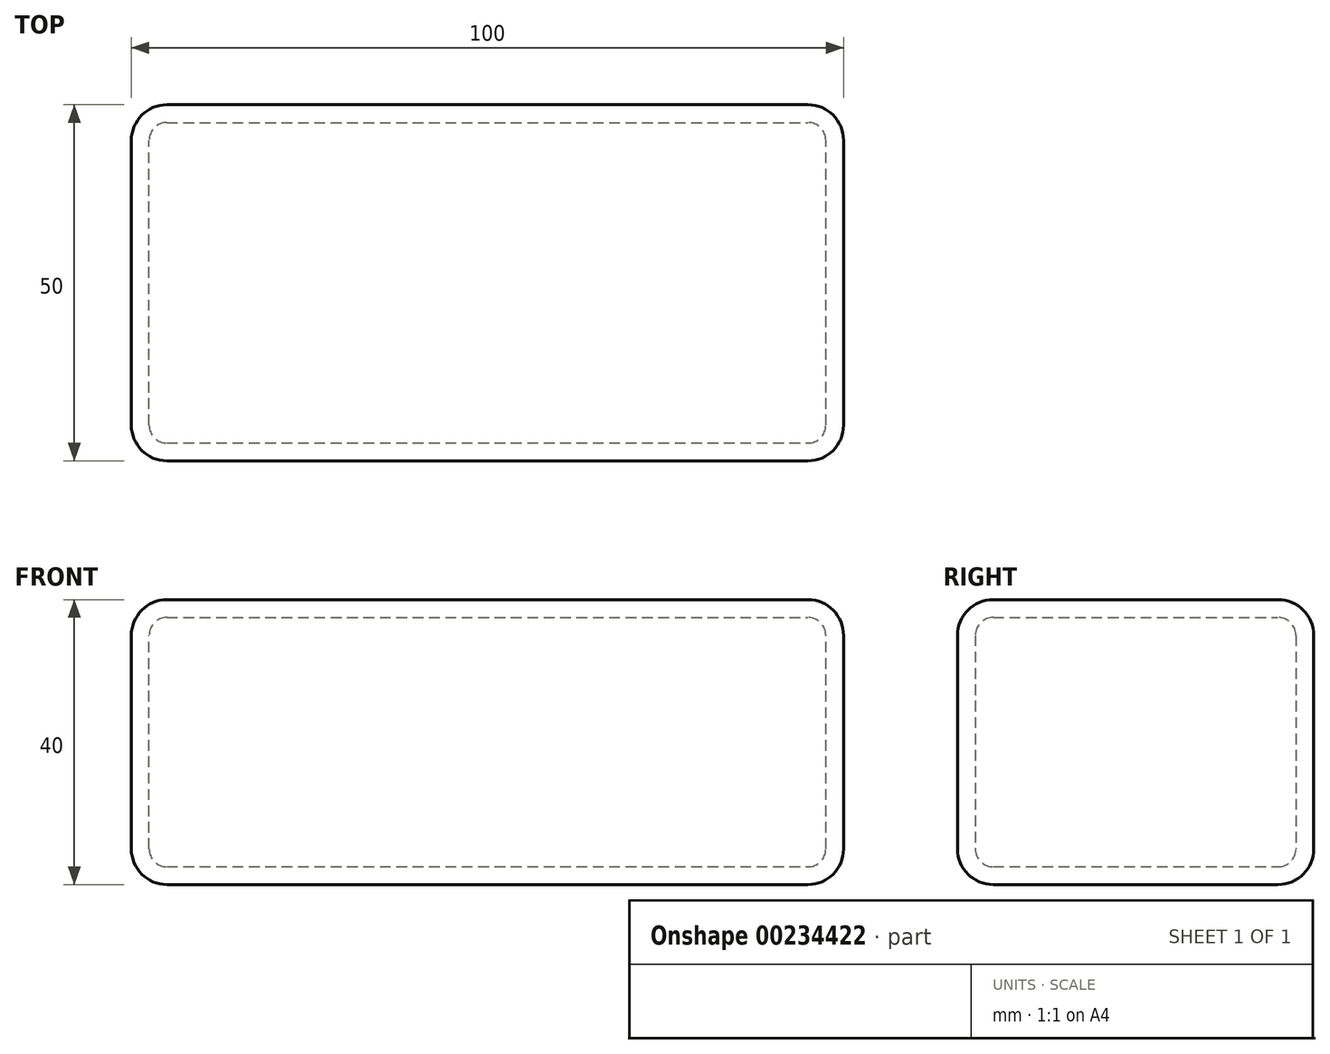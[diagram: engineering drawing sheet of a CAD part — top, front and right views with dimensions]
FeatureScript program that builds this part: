
annotation { "Feature Type Name" : "Feature", "Feature Type Description" : "" }
export const myFeature = defineFeature(function(context is Context, id is Id, definition is map)
    precondition{}
    {
        {
            var Q0;
            Q0=qCreatedBy(makeId("Top.planeOp"),FACE);
            var sketch = newSketch(context, id + "F0", { "sketchPlane" : qUnion([Q0])});
            skLineSegment(sketch, "E0.bottom", {"start": v(50, -25) * mm, "end": v(-50, -25) * mm});
            skLineSegment(sketch, "E0.top", {"start": v(50, 25) * mm, "end": v(-50, 25) * mm});
            skLineSegment(sketch, "E0.left", {"start": v(50, -25) * mm, "end": v(50, 25) * mm});
            skLineSegment(sketch, "E0.right", {"start": v(-50, -25) * mm, "end": v(-50, 25) * mm});
            skPoint(sketch, "E0.middle", {"position": v(0, 0) * mm});
            skSolve(sketch);
        }
        {
            var Q0;
            Q0=makeQuery(id+"F0.imprint","IMPRINT",FACE,{"disambiguationData":[TD([[makeQuery(id+"F0.imprint","IMPRINT",EDGE,{"derivedFrom":sQuery(id+"F0.wireOp",EDGE,"E0.bottom")}),-1.0]])]});
            extrude(context, id + "F1", {"entities" : qUnion([Q0]), "depth" : 20 * mm});
        }
        {
            var Q0;
            Q0=makeQuery(id+"F1.opExtrude","CAP_EDGE",EDGE,{"disambiguationData":[OSD([sQuery(id+"F0.wireOp",EDGE,"E0.right")])],"isStart":false});
            var Q1;
            Q1=makeQuery(id+"F1.opExtrude","CAP_EDGE",EDGE,{"disambiguationData":[OSD([sQuery(id+"F0.wireOp",EDGE,"E0.bottom")])],"isStart":false});
            var Q2;
            Q2=makeQuery(id+"F1.opExtrude","CAP_EDGE",EDGE,{"disambiguationData":[OSD([sQuery(id+"F0.wireOp",EDGE,"E0.left")])],"isStart":false});
            var Q3;
            Q3=makeQuery(id+"F1.opExtrude","CAP_EDGE",EDGE,{"disambiguationData":[OSD([sQuery(id+"F0.wireOp",EDGE,"E0.top")])],"isStart":false});
            var Q4;
            Q4=makeQuery(id+"F1.opExtrude","SWEPT_EDGE",EDGE,{"disambiguationData":[OSD([sQuery(id+"F0.wireOp",EDGE,"E0.top"),sQuery(id+"F0.wireOp",EDGE,"E0.left")])]});
            var Q5;
            Q5=makeQuery(id+"F1.opExtrude","SWEPT_EDGE",EDGE,{"disambiguationData":[OSD([sQuery(id+"F0.wireOp",EDGE,"E0.bottom"),sQuery(id+"F0.wireOp",EDGE,"E0.left")])]});
            var Q6;
            Q6=makeQuery(id+"F1.opExtrude","SWEPT_EDGE",EDGE,{"disambiguationData":[OSD([sQuery(id+"F0.wireOp",EDGE,"E0.bottom"),sQuery(id+"F0.wireOp",EDGE,"E0.right")])]});
            var Q7;
            Q7=makeQuery(id+"F1.opExtrude","SWEPT_EDGE",EDGE,{"disambiguationData":[OSD([sQuery(id+"F0.wireOp",EDGE,"E0.top"),sQuery(id+"F0.wireOp",EDGE,"E0.right")])]});
            fillet(context, id + "F2", {"entities" : qUnion([Q0, Q1, Q2, Q3, Q4, Q5, Q6, Q7]), "radius" : 5 * mm, "tangentPropagation" : true, "allowEdgeOverflow" : false});
        }
        {
            var Q0;
            Q0=makeQuery(id+"F1.opExtrude","CAP_FACE",FACE,{"disambiguationData":[OSD([sQuery(id+"F0.wireOp",EDGE,"E0.bottom"),sQuery(id+"F0.wireOp",EDGE,"E0.top"),sQuery(id+"F0.wireOp",EDGE,"E0.left"),sQuery(id+"F0.wireOp",EDGE,"E0.right")])],"isStart":true});
            shell(context, id + "F3", {"entities" : qUnion([Q0]), "thickness" : 2.5 * mm});
        }
        {
            var Q0;
            Q0=makeQuery(id+"F1.opExtrude","SWEPT_BODY",BODY,{"disambiguationData":[OSD([sQuery(id+"F0.wireOp",EDGE,"E0.bottom"),sQuery(id+"F0.wireOp",EDGE,"E0.top"),sQuery(id+"F0.wireOp",EDGE,"E0.left"),sQuery(id+"F0.wireOp",EDGE,"E0.right")])]});
            var Q1;
            Q1=qCreatedBy(makeId("Top.planeOp"),FACE);
            mirror(context, id + "F4", {"operationType" : NewBodyOperationType.ADD, "entities" : qUnion([Q0]), "mirrorPlane" : qUnion([Q1])});
        }
    });
